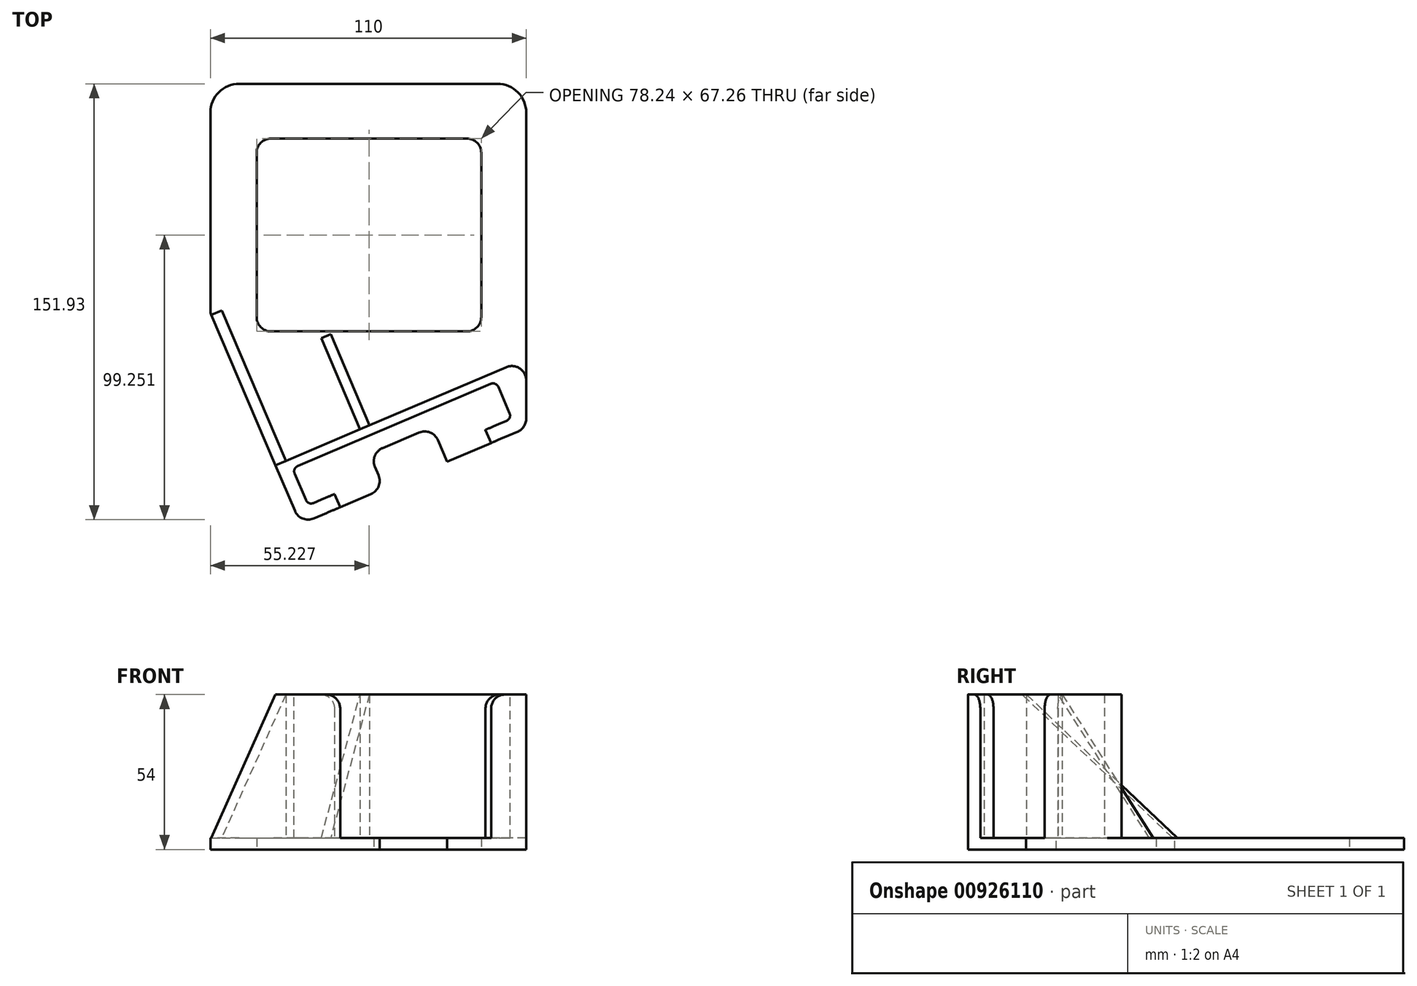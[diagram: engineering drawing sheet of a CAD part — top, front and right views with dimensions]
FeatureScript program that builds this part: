
annotation { "Feature Type Name" : "Feature", "Feature Type Description" : "" }
export const myFeature = defineFeature(function(context is Context, id is Id, definition is map)
    precondition{}
    {
        {
            var Q0;
            Q0=qCreatedBy(makeId("Top.planeOp"),FACE);
            var sketch = newSketch(context, id + "F0", { "sketchPlane" : qUnion([Q0])});
            skLineSegment(sketch, "E0.bottom", {"start": v(-40.19, 22.01) * mm, "end": v(49.81, 22.01) * mm});
            skLineSegment(sketch, "E0.top", {"start": v(-50.19, -97.99) * mm, "end": v(59.81, -97.99) * mm});
            skLineSegment(sketch, "E0.left", {"start": v(-50.19, 12.01) * mm, "end": v(-50.19, -97.99) * mm});
            skLineSegment(sketch, "E0.right", {"start": v(59.81, 12.01) * mm, "end": v(59.81, -97.99) * mm});
            skPoint(sketch, "E1.visualSharp", {"position": v(-50.19, 22.01) * mm});
            skArc(sketch, "E1.filletArc", {"start": v(-40.19, 22.01) * mm, "mid": v(-47.26, 19.08) * mm, "end": v(-50.19, 12.01) * mm});
            skPoint(sketch, "E2.visualSharp", {"position": v(59.81, 22.01) * mm});
            skArc(sketch, "E2.filletArc", {"start": v(59.81, 12.01) * mm, "mid": v(56.88, 19.08) * mm, "end": v(49.81, 22.01) * mm});
            skLineSegment(sketch, "E3", {"start": v(-34.08, -2.04) * mm, "end": v(-34.08, -59.3) * mm});
            skLineSegment(sketch, "E4.MirrorCS", {"start": v(44.16, -2.04) * mm, "end": v(44.16, -59.3) * mm});
            skLineSegment(sketch, "E5", {"start": v(-29.08, 2.96) * mm, "end": v(39.16, 2.96) * mm});
            skLineSegment(sketch, "E6", {"start": v(39.16, -64.3) * mm, "end": v(-29.08, -64.3) * mm});
            skPoint(sketch, "E7.visualSharp", {"position": v(-34.08, 2.96) * mm});
            skArc(sketch, "E7.filletArc", {"start": v(-29.08, 2.96) * mm, "mid": v(-32.62, 1.5) * mm, "end": v(-34.08, -2.04) * mm});
            skPoint(sketch, "E8.visualSharp", {"position": v(44.16, 2.96) * mm});
            skArc(sketch, "E8.filletArc", {"start": v(44.16, -2.04) * mm, "mid": v(42.7, 1.5) * mm, "end": v(39.16, 2.96) * mm});
            skPoint(sketch, "E9.visualSharp", {"position": v(44.16, -64.3) * mm});
            skArc(sketch, "E9.filletArc", {"start": v(39.16, -64.3) * mm, "mid": v(42.7, -62.83) * mm, "end": v(44.16, -59.3) * mm});
            skPoint(sketch, "E10.visualSharp", {"position": v(-34.08, -64.3) * mm});
            skArc(sketch, "E10.filletArc", {"start": v(-34.08, -59.3) * mm, "mid": v(-32.62, -62.83) * mm, "end": v(-29.08, -64.3) * mm});
            skLineSegment(sketch, "E11", {"start": v(59.81, -97.99) * mm, "end": v(-18.8, -131.48) * mm});
            skLineSegment(sketch, "E12", {"start": v(-18.8, -131.48) * mm, "end": v(-33.07, -97.99) * mm});
            skSolve(sketch);
        }
        {
            var Q0;
            Q0=makeQuery(id+"F0.imprint","IMPRINT",FACE,{"disambiguationData":[TD([[makeQuery(id+"F0.imprint","IMPRINT",EDGE,{"derivedFrom":sQuery(id+"F0.wireOp",EDGE,"E0.bottom")}),-1.0]])]});
            var Q1;
            {var subQ0=sQuery(id+"F0.wireOp",EDGE,"E11");Q1=makeQuery(id+"F0.imprint","IMPRINT",FACE,{"disambiguationData":[TD([[makeQuery(id+"F0.imprint","IMPRINT",EDGE,{"derivedFrom":subQ0}),-1.0]])]});}
            extrude(context, id + "F1", {"entities" : qUnion([Q0, Q1]), "depth" : 4 * mm, "offsetDistance" : 25 * mm});
        }
        {
            var Q0;
            Q0=makeQuery(id+"F1.opExtrude","SWEPT_EDGE",EDGE,{"disambiguationData":[OSD([sQuery(id+"F0.wireOp",EDGE,"E0.top"),sQuery(id+"F0.wireOp",EDGE,"E12")])]});
            var Q1;
            Q1=makeQuery(id+"F1.opExtrude","SWEPT_EDGE",EDGE,{"disambiguationData":[OSD([sQuery(id+"F0.wireOp",EDGE,"E0.top"),sQuery(id+"F0.wireOp",EDGE,"E0.left")])]});
            var Q2;
            Q2=makeQuery(id+"F1.opExtrude","SWEPT_EDGE",EDGE,{"disambiguationData":[OSD([sQuery(id+"F0.wireOp",EDGE,"E0.top"),sQuery(id+"F0.wireOp",EDGE,"E0.right"),sQuery(id+"F0.wireOp",EDGE,"E11")])]});
            var Q3;
            Q3=makeQuery(id+"F1.opExtrude","SWEPT_EDGE",EDGE,{"disambiguationData":[OSD([sQuery(id+"F0.wireOp",EDGE,"E11"),sQuery(id+"F0.wireOp",EDGE,"E12")])]});
            fillet(context, id + "F2", {"entities" : qUnion([Q0, Q1, Q2, Q3]), "radius" : 5 * mm, "tangentPropagation" : true, "allowEdgeOverflow" : false});
        }
        {
            var Q0;
            Q0=makeQuery(id+"F1.opExtrude","CAP_FACE",FACE,{"disambiguationData":[OSD([sQuery(id+"F0.wireOp",EDGE,"E0.bottom"),sQuery(id+"F0.wireOp",EDGE,"E0.top"),sQuery(id+"F0.wireOp",EDGE,"E0.left"),sQuery(id+"F0.wireOp",EDGE,"E0.right"),sQuery(id+"F0.wireOp",EDGE,"E1.filletArc"),sQuery(id+"F0.wireOp",EDGE,"E2.filletArc"),sQuery(id+"F0.wireOp",EDGE,"E3"),sQuery(id+"F0.wireOp",EDGE,"E4.MirrorCS"),sQuery(id+"F0.wireOp",EDGE,"E5"),sQuery(id+"F0.wireOp",EDGE,"E6"),sQuery(id+"F0.wireOp",EDGE,"E7.filletArc"),sQuery(id+"F0.wireOp",EDGE,"E8.filletArc"),sQuery(id+"F0.wireOp",EDGE,"E9.filletArc"),sQuery(id+"F0.wireOp",EDGE,"E10.filletArc"),sQuery(id+"F0.wireOp",EDGE,"E11"),sQuery(id+"F0.wireOp",EDGE,"E12")])],"isStart":false});
            var sketch = newSketch(context, id + "F3", { "sketchPlane" : qUnion([Q0])});
            skLineSegment(sketch, "E13", {"start": v(-16.17, -124.92) * mm, "end": v(54.81, -94.68) * mm});
            skLineSegment(sketch, "E14", {"start": v(54.81, -94.68) * mm, "end": v(49.33, -81.8) * mm});
            skLineSegment(sketch, "E15", {"start": v(-16.17, -124.92) * mm, "end": v(-21.65, -112.04) * mm});
            skLineSegment(sketch, "E16", {"start": v(-21.65, -112.04) * mm, "end": v(49.33, -81.8) * mm});
            skLineSegment(sketch, "E17", {"start": v(-27.53, -111) * mm, "end": v(59.81, -73.8) * mm});
            skLineSegment(sketch, "E18", {"start": v(-6.97, -121) * mm, "end": v(-5, -125.6) * mm});
            skLineSegment(sketch, "E19", {"start": v(47.57, -103.2) * mm, "end": v(45.61, -98.6) * mm});
            skLineSegment(sketch, "E20", {"start": v(-27.53, -111) * mm, "end": v(-49.87, -58.55) * mm});
            skLineSegment(sketch, "E21", {"start": v(-49.87, -58.55) * mm, "end": v(-46.29, -57.02) * mm});
            skLineSegment(sketch, "E22", {"start": v(-46.29, -57.02) * mm, "end": v(-23.94, -109.48) * mm});
            skLineSegment(sketch, "E23", {"start": v(1.93, -98.46) * mm, "end": v(-11.6, -66.72) * mm});
            skLineSegment(sketch, "E24", {"start": v(5.2, -97.07) * mm, "end": v(-8.44, -65.03) * mm});
            skLineSegment(sketch, "E25", {"start": v(-11.6, -66.72) * mm, "end": v(-8.32, -65.32) * mm});
            skSolve(sketch);
        }
        {
            var Q0;
            {var subQ13=sQuery(id+"F3.wireOp",EDGE,"E14");Q0=makeQuery(id+"F3.imprint","IMPRINT",FACE,{"disambiguationData":[TD([[makeQuery(id+"F3.imprint","IMPRINT",EDGE,{"derivedFrom":subQ13}),-1.0]])]});}
            var Q1;
            {var subQ0=sQuery(id+"F3.wireOp",EDGE,"E21");Q1=makeQuery(id+"F3.imprint","IMPRINT",FACE,{"disambiguationData":[TD([[makeQuery(id+"F3.imprint","IMPRINT",EDGE,{"derivedFrom":subQ0}),-1.0]])]});}
            var Q2;
            {var subQ0=sQuery(id+"F3.wireOp",EDGE,"E23");Q2=makeQuery(id+"F3.imprint","IMPRINT",FACE,{"disambiguationData":[TD([[makeQuery(id+"F3.imprint","IMPRINT",EDGE,{"derivedFrom":subQ0}),-1.0]])]});}
            extrude(context, id + "F4", {"entities" : qUnion([Q0, Q1, Q2]), "operationType" : NewBodyOperationType.ADD, "depth" : 50 * mm, "offsetDistance" : 25 * mm});
        }
        {
            var Q0;
            {var subQ5=sQuery(id+"F0.wireOp",EDGE,"E11");var subQ7=sQuery(id+"F0.wireOp",EDGE,"E12");var subQ8=sQuery(id+"F0.wireOp",EDGE,"E0.right");var subQ9=sQuery(id+"F0.wireOp",EDGE,"E0.top");var subQ10=makeQuery(id+"F1.opExtrude","CAP_FACE",FACE,{"disambiguationData":[OSD([sQuery(id+"F0.wireOp",EDGE,"E0.bottom"),subQ9,sQuery(id+"F0.wireOp",EDGE,"E0.left"),subQ8,sQuery(id+"F0.wireOp",EDGE,"E1.filletArc"),sQuery(id+"F0.wireOp",EDGE,"E2.filletArc"),sQuery(id+"F0.wireOp",EDGE,"E3"),sQuery(id+"F0.wireOp",EDGE,"E4.MirrorCS"),sQuery(id+"F0.wireOp",EDGE,"E5"),sQuery(id+"F0.wireOp",EDGE,"E6"),sQuery(id+"F0.wireOp",EDGE,"E7.filletArc"),sQuery(id+"F0.wireOp",EDGE,"E8.filletArc"),sQuery(id+"F0.wireOp",EDGE,"E9.filletArc"),sQuery(id+"F0.wireOp",EDGE,"E10.filletArc"),subQ5,subQ7])],"isStart":false});Q0=makeQuery(id+"F4.boolean.opBoolean","SPLIT",FACE,{"disambiguationData":[TD([makeQuery(id+"F1.opExtrude","SWEPT_FACE",FACE,{"disambiguationData":[OSD([subQ5])]})])],"derivedFrom":subQ10});}
            var sketch = newSketch(context, id + "F5", { "sketchPlane" : qUnion([Q0])});
            skLineSegment(sketch, "E26", {"start": v(21.28, -114.4) * mm, "end": v(16.11, -102.26) * mm});
            skLineSegment(sketch, "E27", {"start": v(16.11, -102.26) * mm, "end": v(27.07, -97.6) * mm});
            skLineSegment(sketch, "E28", {"start": v(27.07, -97.6) * mm, "end": v(32.24, -109.73) * mm});
            skLineSegment(sketch, "E29.MirrorCS", {"start": v(16.11, -102.26) * mm, "end": v(5.16, -106.93) * mm});
            skLineSegment(sketch, "E30.MirrorCS", {"start": v(5.16, -106.93) * mm, "end": v(10.33, -119.07) * mm});
            skSolve(sketch);
        }
        {
            var Q0;
            {var subQ0=sQuery(id+"F5.wireOp",EDGE,"E26");Q0=makeQuery(id+"F5.imprint","IMPRINT",FACE,{"disambiguationData":[TD([[makeQuery(id+"F5.imprint","IMPRINT",EDGE,{"derivedFrom":subQ0}),1.0]])]});}
            var Q1;
            {var subQ0=sQuery(id+"F5.wireOp",EDGE,"E26");Q1=makeQuery(id+"F5.imprint","IMPRINT",FACE,{"disambiguationData":[TD([[makeQuery(id+"F5.imprint","IMPRINT",EDGE,{"derivedFrom":subQ0}),-1.0]])]});}
            extrude(context, id + "F6", {"entities" : qUnion([Q0, Q1]), "operationType" : NewBodyOperationType.REMOVE, "oppositeDirection" : true, "depth" : 25 * mm, "offsetDistance" : 25 * mm});
        }
        {
            var Q0;
            Q0=makeQuery(id+"F4.opExtrude","CAP_EDGE",EDGE,{"disambiguationData":[OSD([sQuery(id+"F3.wireOp",EDGE,"E18")])],"isStart":false});
            var Q1;
            Q1=makeQuery(id+"F4.opExtrude","CAP_EDGE",EDGE,{"disambiguationData":[OSD([sQuery(id+"F3.wireOp",EDGE,"E19")])],"isStart":false});
            var Q2;
            Q2=makeQuery(id+"F4.opExtrude","CAP_EDGE",EDGE,{"disambiguationData":[OSD([sQuery(id+"F3.wireOp",EDGE,"E19")])],"isStart":true});
            var Q3;
            Q3=makeQuery(id+"F4.opExtrude","CAP_EDGE",EDGE,{"disambiguationData":[OSD([sQuery(id+"F3.wireOp",EDGE,"E18")])],"isStart":true});
            var Q4;
            Q4=makeQuery(id+"F6.boolean.opBoolean","COPY",EDGE,{"derivedFrom":makeQuery(id+"F6.opExtrude","SWEPT_EDGE",EDGE,{"disambiguationData":[OSD([sQuery(id+"F0.wireOp",EDGE,"E11"),sQuery(id+"F5.wireOp",EDGE,"E28")])]})});
            var Q5;
            Q5=makeQuery(id+"F6.boolean.opBoolean","COPY",EDGE,{"derivedFrom":makeQuery(id+"F6.opExtrude","SWEPT_EDGE",EDGE,{"disambiguationData":[OSD([sQuery(id+"F0.wireOp",EDGE,"E11"),sQuery(id+"F5.wireOp",EDGE,"E30.MirrorCS")])]})});
            var Q6;
            Q6=makeQuery(id+"F6.boolean.opBoolean","COPY",EDGE,{"derivedFrom":makeQuery(id+"F6.opExtrude","SWEPT_EDGE",EDGE,{"disambiguationData":[OSD([sQuery(id+"F5.wireOp",EDGE,"E27"),sQuery(id+"F5.wireOp",EDGE,"E28")])]})});
            var Q7;
            Q7=makeQuery(id+"F6.boolean.opBoolean","COPY",EDGE,{"derivedFrom":makeQuery(id+"F6.opExtrude","SWEPT_EDGE",EDGE,{"disambiguationData":[OSD([sQuery(id+"F5.wireOp",EDGE,"E29.MirrorCS"),sQuery(id+"F5.wireOp",EDGE,"E30.MirrorCS")])]})});
            fillet(context, id + "F7", {"entities" : qUnion([Q0, Q1, Q2, Q3, Q4, Q5, Q6, Q7]), "radius" : 5 * mm, "tangentPropagation" : true, "allowEdgeOverflow" : false});
        }
        {
            var Q0;
            Q0=makeQuery(id+"F4.opExtrude","SWEPT_EDGE",EDGE,{"disambiguationData":[OSD([sQuery(id+"F3.wireOp",EDGE,"E14"),sQuery(id+"F3.wireOp",EDGE,"E16")])]});
            var Q1;
            Q1=makeQuery(id+"F4.opExtrude","SWEPT_EDGE",EDGE,{"disambiguationData":[OSD([sQuery(id+"F3.wireOp",EDGE,"E13"),sQuery(id+"F3.wireOp",EDGE,"E14")])]});
            var Q2;
            Q2=makeQuery(id+"F4.opExtrude","SWEPT_EDGE",EDGE,{"disambiguationData":[OSD([sQuery(id+"F3.wireOp",EDGE,"E15"),sQuery(id+"F3.wireOp",EDGE,"E16")])]});
            var Q3;
            Q3=makeQuery(id+"F4.opExtrude","SWEPT_EDGE",EDGE,{"disambiguationData":[OSD([sQuery(id+"F3.wireOp",EDGE,"E13"),sQuery(id+"F3.wireOp",EDGE,"E15")])]});
            fillet(context, id + "F8", {"entities" : qUnion([Q0, Q1, Q2, Q3]), "radius" : 2 * mm, "tangentPropagation" : true, "allowEdgeOverflow" : false});
        }
        {
            var Q0;
            Q0=makeQuery(id+"F4.opExtrude","SWEPT_FACE",FACE,{"disambiguationData":[OSD([sQuery(id+"F3.wireOp",EDGE,"E22")])]});
            var sketch = newSketch(context, id + "F9", { "sketchPlane" : qUnion([Q0])});
            skLineSegment(sketch, "E31", {"start": v(-91.34, 54) * mm, "end": v(-34.32, 4) * mm});
            skSolve(sketch);
        }
        {
            var Q0;
            Q0=makeQuery(id+"F9.imprint","IMPRINT",FACE,{"disambiguationData":[TD([[makeQuery(id+"F9.imprint","IMPRINT",EDGE,{"derivedFrom":sQuery(id+"F9.wireOp",EDGE,"E31")}),1.0]])]});
            extrude(context, id + "F10", {"entities" : qUnion([Q0]), "operationType" : NewBodyOperationType.REMOVE, "oppositeDirection" : true, "depth" : 25 * mm, "offsetDistance" : 25 * mm});
        }
        {
            var Q0;
            {var subQ0=sQuery(id+"F0.wireOp",EDGE,"E5");var subQ1=sQuery(id+"F0.wireOp",EDGE,"E4.MirrorCS");var subQ2=sQuery(id+"F0.wireOp",EDGE,"E0.left");var subQ3=sQuery(id+"F0.wireOp",EDGE,"E0.top");var subQ4=sQuery(id+"F0.wireOp",EDGE,"E3");var subQ5=sQuery(id+"F0.wireOp",EDGE,"E2.filletArc");var subQ6=sQuery(id+"F0.wireOp",EDGE,"E0.right");var subQ7=sQuery(id+"F0.wireOp",EDGE,"E1.filletArc");var subQ8=sQuery(id+"F0.wireOp",EDGE,"E6");var subQ9=sQuery(id+"F0.wireOp",EDGE,"E0.bottom");var subQ10=sQuery(id+"F0.wireOp",EDGE,"E12");var subQ11=sQuery(id+"F0.wireOp",EDGE,"E7.filletArc");var subQ12=sQuery(id+"F0.wireOp",EDGE,"E8.filletArc");var subQ13=sQuery(id+"F0.wireOp",EDGE,"E9.filletArc");var subQ14=sQuery(id+"F0.wireOp",EDGE,"E10.filletArc");Q0=makeQuery(id+"F4.boolean.opBoolean","SPLIT",FACE,{"disambiguationData":[TD([makeQuery(id+"F1.opExtrude","SWEPT_FACE",FACE,{"disambiguationData":[OSD([subQ9])]})])],"derivedFrom":makeQuery(id+"F1.opExtrude","CAP_FACE",FACE,{"disambiguationData":[OSD([subQ9,subQ3,subQ2,subQ6,subQ7,subQ5,subQ4,subQ1,subQ0,subQ8,subQ11,subQ12,subQ13,subQ14,sQuery(id+"F0.wireOp",EDGE,"E11"),subQ10])],"isStart":false})});}
            var sketch = newSketch(context, id + "F11", { "sketchPlane" : qUnion([Q0])});
            skLineSegment(sketch, "E32", {"start": v(-31.78, -101.03) * mm, "end": v(-50.19, -57.8) * mm});
            skSolve(sketch);
        }
        {
            var Q0;
            {var subQ2=sQuery(id+"F0.wireOp",EDGE,"E0.top");Q0=makeQuery(id+"F11.imprint","IMPRINT",FACE,{"disambiguationData":[TD([[makeQuery(id+"F11.imprint","IMPRINT",EDGE,{"derivedFrom":makeQuery(id+"F1.opExtrude","CAP_EDGE",EDGE,{"disambiguationData":[OSD([subQ2])],"isStart":false})}),1.0]])]});}
            extrude(context, id + "F12", {"entities" : qUnion([Q0]), "operationType" : NewBodyOperationType.REMOVE, "oppositeDirection" : true, "depth" : 25 * mm, "offsetDistance" : 25 * mm});
        }
        {
            var Q0;
            Q0=makeQuery(id+"F4.opExtrude","SWEPT_FACE",FACE,{"disambiguationData":[OSD([sQuery(id+"F3.wireOp",EDGE,"E24")])]});
            var sketch = newSketch(context, id + "F13", { "sketchPlane" : qUnion([Q0])});
            skLineSegment(sketch, "E33", {"start": v(-91.34, 54) * mm, "end": v(-56.84, 4) * mm});
            skSolve(sketch);
        }
        {
            var Q0;
            Q0=makeQuery(id+"F13.imprint","IMPRINT",FACE,{"disambiguationData":[TD([[makeQuery(id+"F13.imprint","IMPRINT",EDGE,{"derivedFrom":sQuery(id+"F13.wireOp",EDGE,"E33")}),1.0]])]});
            extrude(context, id + "F14", {"entities" : qUnion([Q0]), "operationType" : NewBodyOperationType.REMOVE, "oppositeDirection" : true, "depth" : 25 * mm, "offsetDistance" : 25 * mm});
        }
        {
            var Q0;
            Q0=makeQuery(id+"F4.opExtrude","SWEPT_EDGE",EDGE,{"disambiguationData":[OSD([sQuery(id+"F0.wireOp",EDGE,"E0.right"),sQuery(id+"F3.wireOp",EDGE,"E17")])]});
            fillet(context, id + "F15", {"entities" : qUnion([Q0]), "radius" : 5 * mm, "tangentPropagation" : true, "allowEdgeOverflow" : false});
        }
    });
